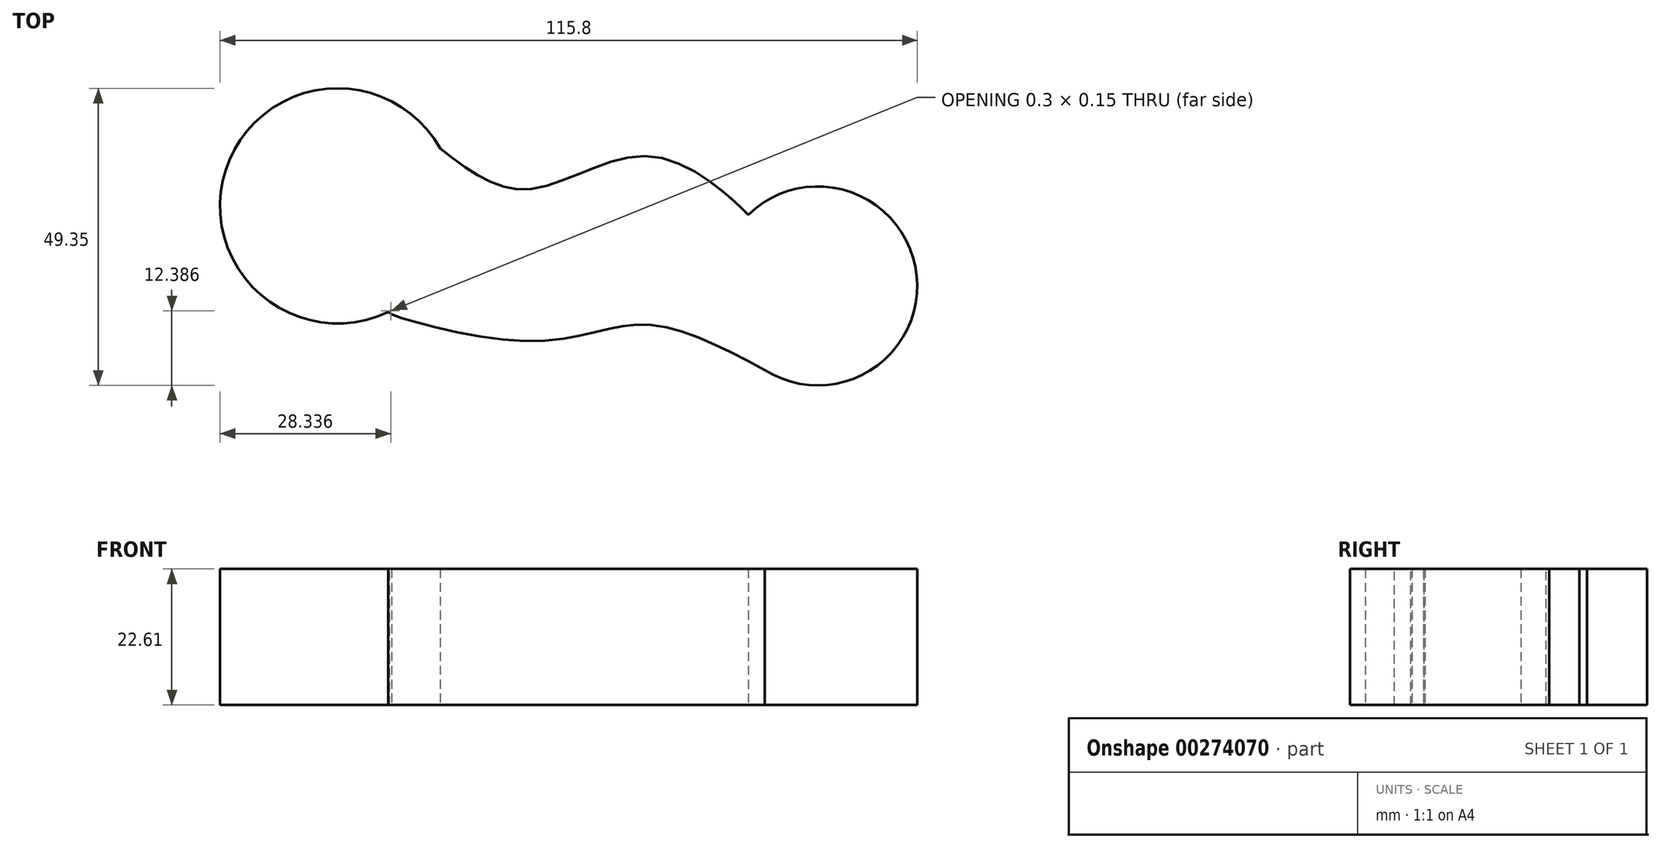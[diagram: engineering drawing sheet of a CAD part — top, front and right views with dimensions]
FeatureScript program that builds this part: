
annotation { "Feature Type Name" : "Feature", "Feature Type Description" : "" }
export const myFeature = defineFeature(function(context is Context, id is Id, definition is map)
    precondition{}
    {
        {
            var Q0;
            Q0=qCreatedBy(makeId("Top.planeOp"),FACE);
            var sketch = newSketch(context, id + "F0", { "sketchPlane" : qUnion([Q0])});
            skCircle(sketch, "E0", {"center": v(-46.56, 36.32) * mm, "radius": 19.53 * mm});
            skFitSpline(sketch, "E1", {"points": [v(-29.52, 45.86) * mm, v(-14.85, 39.08) * mm, v(6.53, 44.43) * mm, v(21.28, 35.21) * mm, v(21.65, 34.84) * mm], "startDerivative": vector(46.8, -36.67) * mm, "endDerivative": vector(3.9, -3.86) * mm});
            skCircle(sketch, "E2", {"center": v(33.19, 23.02) * mm, "radius": 16.52 * mm});
            skPoint(sketch, "E2.first.point", {"position": v(16.67, 22.68) * mm});
            skPoint(sketch, "E2.third.point", {"position": v(47.46, 31.34) * mm});
            skFitSpline(sketch, "E3", {"points": [v(26.23, 8.04) * mm, v(4.5, 16.6) * mm, v(-14.85, 13.83) * mm, v(-38.2, 18.67) * mm, v(-37.9, 18.81) * mm, v(-37.6, 18.96) * mm], "startDerivative": vector(-72.45, 39.52) * mm, "endDerivative": vector(6.6, 4.4) * mm});
            skSolve(sketch);
        }
        {
            var Q0;
            Q0 = qSketchRegion(id + "F0", true);
            extrude(context, id + "F1", {"entities" : qUnion([Q0]), "depth" : 22.6 * mm});
        }
    });
